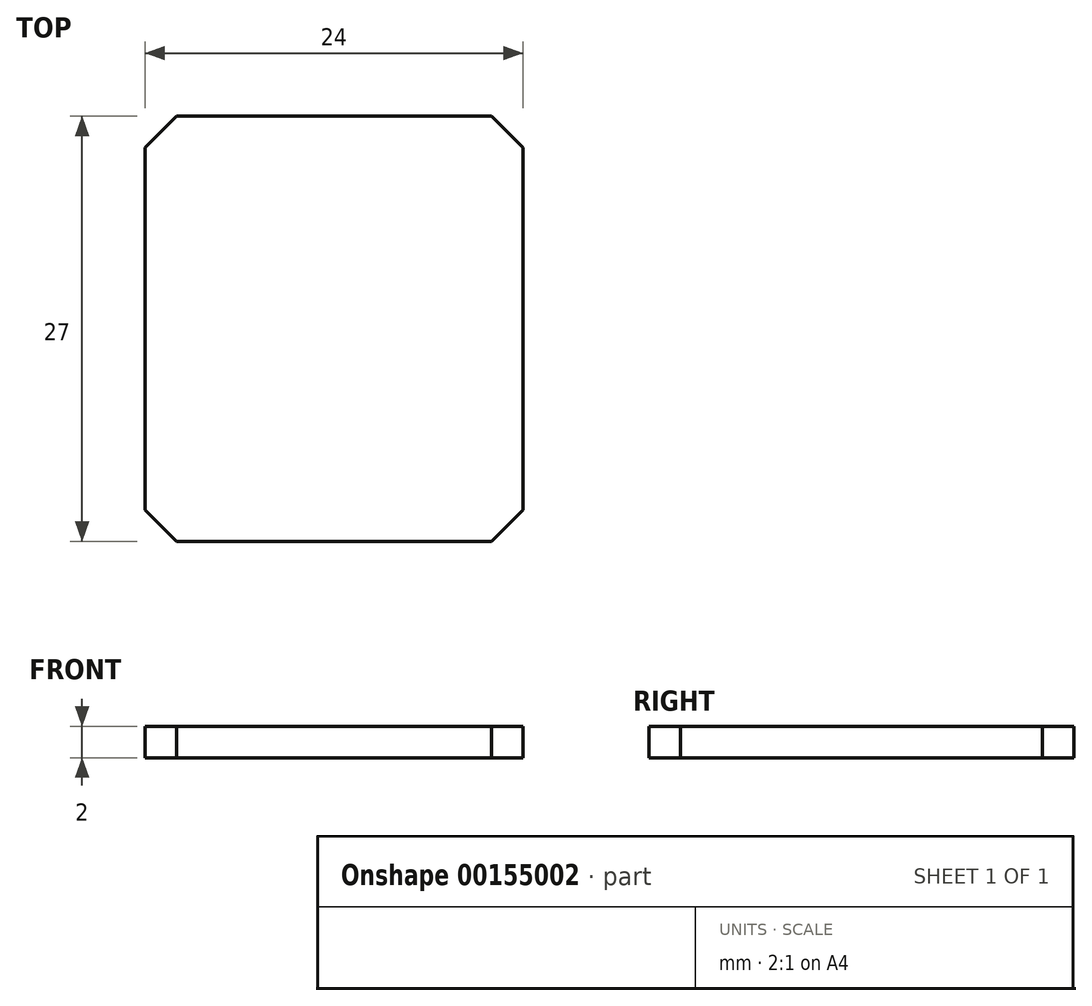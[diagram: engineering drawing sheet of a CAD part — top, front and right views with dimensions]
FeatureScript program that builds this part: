
annotation { "Feature Type Name" : "Feature", "Feature Type Description" : "" }
export const myFeature = defineFeature(function(context is Context, id is Id, definition is map)
    precondition{}
    {
        {
            var Q0;
            Q0=qCreatedBy(makeId("Top.planeOp"),FACE);
            var sketch = newSketch(context, id + "F0", { "sketchPlane" : qUnion([Q0])});
            skLineSegment(sketch, "E0.bottom", {"start": v(12, -13.5) * mm, "end": v(-12, -13.5) * mm});
            skLineSegment(sketch, "E0.top", {"start": v(12, 13.5) * mm, "end": v(-12, 13.5) * mm});
            skLineSegment(sketch, "E0.left", {"start": v(12, -13.5) * mm, "end": v(12, 13.5) * mm});
            skLineSegment(sketch, "E0.right", {"start": v(-12, -13.5) * mm, "end": v(-12, 13.5) * mm});
            skPoint(sketch, "E0.middle", {"position": v(0, 0) * mm});
            skSolve(sketch);
        }
        {
            var Q0;
            Q0=makeQuery(id+"F0.imprint","IMPRINT",FACE,{"disambiguationData":[TD([[makeQuery(id+"F0.imprint","IMPRINT",EDGE,{"derivedFrom":sQuery(id+"F0.wireOp",EDGE,"E0.bottom")}),-1.0]])]});
            extrude(context, id + "F1", {"entities" : qUnion([Q0]), "depth" : 2 * mm});
        }
        {
            var Q0;
            Q0=makeQuery(id+"F1.opExtrude","SWEPT_EDGE",EDGE,{"disambiguationData":[OSD([sQuery(id+"F0.wireOp",EDGE,"E0.top"),sQuery(id+"F0.wireOp",EDGE,"E0.right")])]});
            var Q1;
            Q1=makeQuery(id+"F1.opExtrude","SWEPT_EDGE",EDGE,{"disambiguationData":[OSD([sQuery(id+"F0.wireOp",EDGE,"E0.bottom"),sQuery(id+"F0.wireOp",EDGE,"E0.right")])]});
            var Q2;
            Q2=makeQuery(id+"F1.opExtrude","SWEPT_EDGE",EDGE,{"disambiguationData":[OSD([sQuery(id+"F0.wireOp",EDGE,"E0.bottom"),sQuery(id+"F0.wireOp",EDGE,"E0.left")])]});
            var Q3;
            Q3=makeQuery(id+"F1.opExtrude","SWEPT_EDGE",EDGE,{"disambiguationData":[OSD([sQuery(id+"F0.wireOp",EDGE,"E0.top"),sQuery(id+"F0.wireOp",EDGE,"E0.left")])]});
            chamfer(context, id + "F2", {"entities" : qUnion([Q0, Q1, Q2, Q3]), "width" : 2 * mm, "tangentPropagation" : true});
        }
    });
